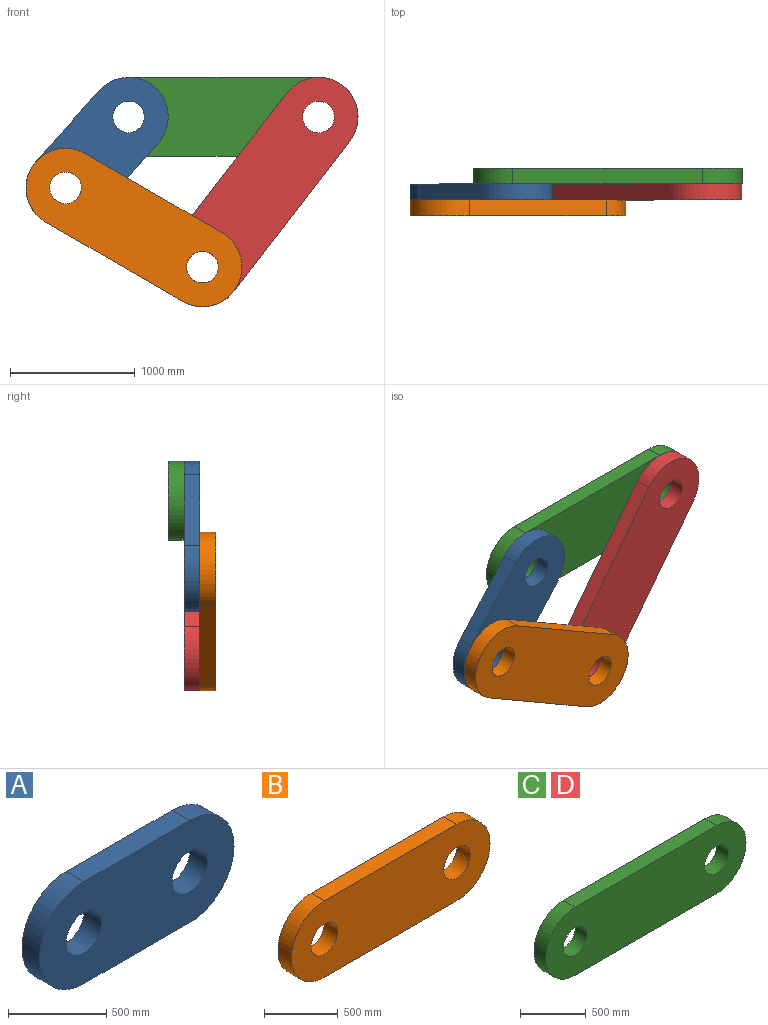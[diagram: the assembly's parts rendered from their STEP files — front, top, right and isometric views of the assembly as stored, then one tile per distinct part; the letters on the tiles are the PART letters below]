
ASSEMBLY  parts=4 mates=7
PART A: 8 faces, bbox 1397x127x635 mm
  f0: cylinder r=317.5mm len=635mm, axis (0,1,0), area 126676.9mm2, adj f1,f5,f6,f7
  f1: plane 762x127mm, normal (0,0,-1), area 96774mm2, adj f0,f2,f6,f7
  f2: cylinder r=317.5mm len=635mm, axis (0,1,0), area 126676.9mm2, adj f1,f5,f6,f7
  f3: cylinder r=127mm len=254mm, axis (0,1,0), area 101341.5mm2, adj f6,f7
  f4: cylinder r=127mm len=254mm, axis (0,1,0), area 101341.5mm2, adj f6,f7
  f5: plane 762x127mm, normal (0,0,1), area 96774mm2, adj f0,f2,f6,f7
  f6: plane 1397x635mm, normal (0,-1,0), area 699220.7mm2, adj f0,f1,f2,f3,f4,f5
  f7: plane 1397x635mm, normal (0,1,0), area 699220.7mm2, adj f0,f1,f2,f3,f4,f5
PART B: 8 faces, bbox 1905x127x635 mm
  f0: cylinder r=317.5mm len=635mm, axis (0,1,0), area 126676.9mm2, adj f1,f5,f6,f7
  f1: plane 1270x127mm, normal (0,0,-1), area 161290mm2, adj f0,f2,f6,f7
  f2: cylinder r=317.5mm len=635mm, axis (0,1,0), area 126676.9mm2, adj f1,f5,f6,f7
  f3: cylinder r=127mm len=254mm, axis (0,1,0), area 101341.5mm2, adj f6,f7
  f4: cylinder r=127mm len=254mm, axis (0,1,0), area 101341.5mm2, adj f6,f7
  f5: plane 1270x127mm, normal (0,0,1), area 161290mm2, adj f0,f2,f6,f7
  f6: plane 1905x635mm, normal (0,-1,0), area 1021800.7mm2, adj f0,f1,f2,f3,f4,f5
  f7: plane 1905x635mm, normal (0,1,0), area 1021800.7mm2, adj f0,f1,f2,f3,f4,f5
PART C: 8 faces, bbox 2159x127x635 mm
  f0: cylinder r=317.5mm len=635mm, axis (0,1,0), area 126676.9mm2, adj f1,f5,f6,f7
  f1: plane 1524x127mm, normal (0,0,-1), area 193548mm2, adj f0,f2,f6,f7
  f2: cylinder r=317.5mm len=635mm, axis (0,1,0), area 126676.9mm2, adj f1,f5,f6,f7
  f3: cylinder r=127mm len=254mm, axis (0,1,0), area 101341.5mm2, adj f6,f7
  f4: cylinder r=127mm len=254mm, axis (0,1,0), area 101341.5mm2, adj f6,f7
  f5: plane 1524x127mm, normal (0,0,1), area 193548mm2, adj f0,f2,f6,f7
  f6: plane 2159x635mm, normal (0,-1,0), area 1183090.7mm2, adj f0,f1,f2,f3,f4,f5
  f7: plane 2159x635mm, normal (0,1,0), area 1183090.7mm2, adj f0,f1,f2,f3,f4,f5
PART D: same geometry as C
PLACE A rot(axis=(0,1,0),131.6deg) t=(-3311.35,-127,1054.46)mm
PLACE B rot(axis=(0,-1,0),149.9deg) t=(-3009.85,-254,445.56)mm
PLACE C t=(-2294.42,0,1335.97)mm fixed
PLACE D rot(axis=(0.44,0,-0.9),180deg) t=(-1999.65,-127,732.09)mm
MATE cylindrical A.f0 <-> C.f0  axis (0,1,0) through (-3057.37,-63.5,1335.97)mm
MATE planar D.f6 <-> C.f6  axis (0,1,0) through (-1999.07,-63.5,732.84)mm
MATE cylindrical A.f2 <-> B.f2  axis (0,1,0) through (-3563.62,-63.5,766.45)mm
MATE cylindrical D.f2 <-> B.f0  axis (0,-1,0) through (-2464.78,-190.5,129.71)mm
MATE planar A.f7 <-> D.f6  axis (0,1,0) through (-3310.5,-63.5,1051.21)mm
MATE cylindrical C.f2 <-> D.f0  axis (0,-1,0) through (-1533.37,-63.5,1335.97)mm
MATE planar D.f7 <-> B.f7  axis (0,-1,0) through (-1999.07,-190.5,732.84)mm
